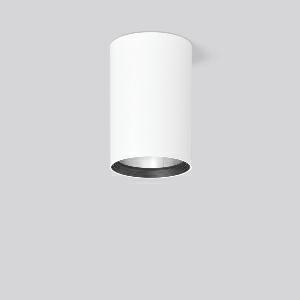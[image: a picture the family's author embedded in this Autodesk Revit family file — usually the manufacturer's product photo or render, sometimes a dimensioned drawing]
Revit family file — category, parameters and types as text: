
# Revit family: heledon_maxi_a_931217_002_1_6182
name_source: partatom
category: Lighting Fixtures
units: mm (PartAtom-declared; Revit-internal decimal feet)

## family parameters
Cut with Voids When Loaded = No
Host = Face
Light Source = No
Part Type = Normal
Room Calculation Point = No
Round Connector Dimension = Use Diameter
Shared = No

## types (1)
- HELEDON maxi A (1 x LED Modul 940, 3500 lm, 4000)
    Apparent Load = 25 VA
    Approval mark = CE
    CIE Flux Codes = 100 100 100 100 100
    Color Rendering = 92
    Color Temperature = 4000
    Default Elevation = 1800 mm
    Description = Series: HELEDON maxi
Cylindrical surface-mounted downlight. Housing: die-cast aluminium, powder-coated. Internal ceiling frame polycarbonate with bayonet mounting. Black plastic ring and recessed LED to prevent glare from the side. Optical assembly with reflector made of MIRO-Silver with 98% total light reflection for outstanding efficiency - can be changed without tools. Best colour rendering index Ra>90. Suitable for Ceiling mounting. Easy installation with a separate ceiling frame with bayonet mounting and plug connection. Driver integrated. Connected via plug-in connector. High quality converter without flickering and stroboscopic effect. The following accessories can be mounted without use of tools: interchangeable lenses, decorative glasses, honeycomb louvre, clear and frosted diffusers, white interchangeable plastic ring. 
Colour: traffic white, matt (RAL 9016)
Diameter: 123 mm
Height: 183 mm
Lamp: LED
Socket: without socket
Colour temperature: 4000K
Colour rendering index (CRI): 92
System power: 25 W
Rated luminous flux: 3500 lm
Luminous efficiency: 140 lm/W
Control gear: Regulated power supply
Protection class: I
Type of protection: IP 20
    Height = 183 mm
    Lamp = 1 x LED Modul 940
    Lamp Light Flux = 3500 lm
    Lamp count = 1
    Length = 123 mm
    Lifetime = 50000 h
    Luminous efficacy = 140 lm/W
    Manufacturer = RZB
    ModVariant = No
    Model = 931217.002.1
    Mounting Place = Ceiling
    Mounting Type = Surface mounted
    Number of Poles = 1
    OnlyDefault = Yes
    Power Factor = 1
    Product Name = HELEDON maxi A
    Product group = Surface mounted downlights
    ProductGroupID = 302
    Protection Class = Protection class I
    Protection Degree = IP 20
    RLX_Detail_Level = 1
    RLX_Emergency_Light_Flux = 0 lm
    RLX_Emergency_Type = 0
    RLX_Emergency_Type_DB = No
    RlxData = <blob elided: 97697 chars, md5=14c33a5c>
    Socket = socket
    Standby Power = 0 W
    System Light Flux = 3500 lm
    System Power = 25 W
    Type Comments = Product without accessories
    Type Image = 931192.002.jpg
    URL = http://relux.com
    VarID = ---
    Voltage = 230 V
    Voltage Range = 220-240 V
    Weight = 0.00 kg
    Width = 0 mm  [stored 0 ft]

note: [stored X ft] marks values corroborated as IEEE doubles in the binary element streams (Revit-internal decimal feet)

## geometry (parser evidence)
native form markers: Blend x4, Sweep x11
no freeform markers — native parametric forms only
